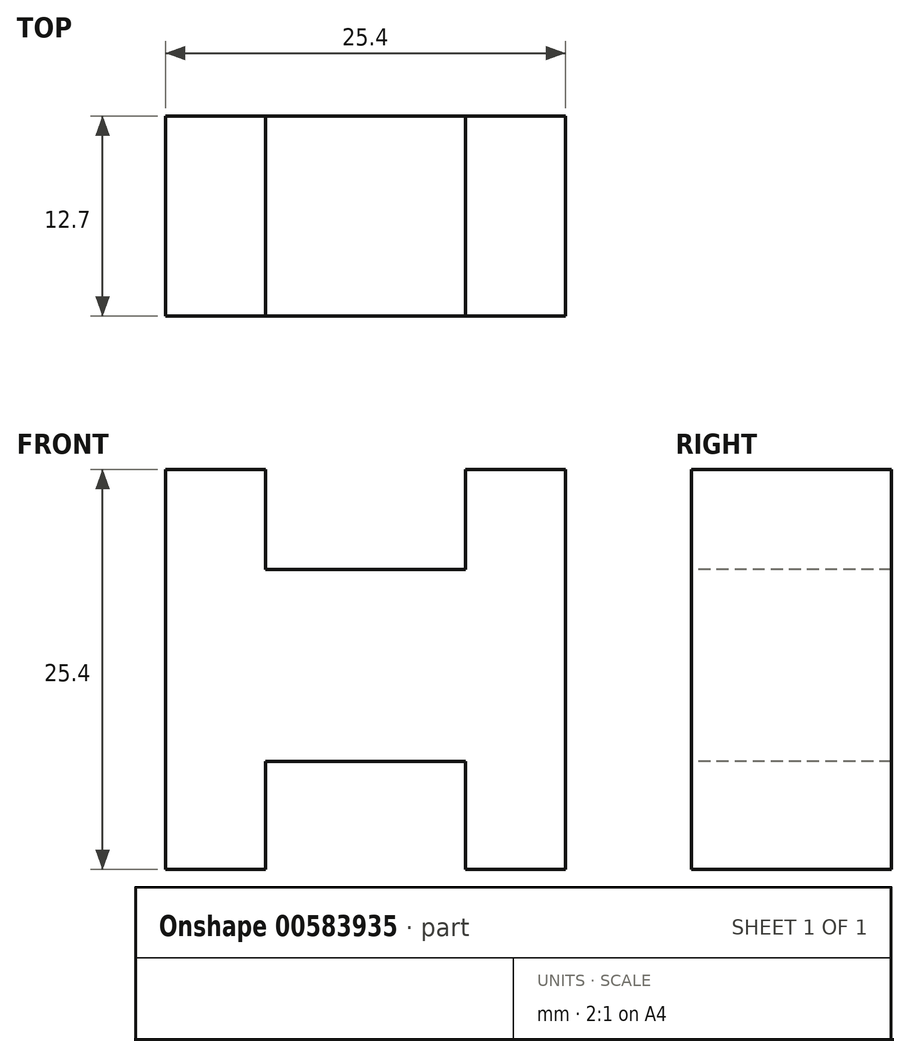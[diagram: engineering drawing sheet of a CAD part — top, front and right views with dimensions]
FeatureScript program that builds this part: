
annotation { "Feature Type Name" : "Feature", "Feature Type Description" : "" }
export const myFeature = defineFeature(function(context is Context, id is Id, definition is map)
    precondition{}
    {
        {
            var Q0;
            Q0=qCreatedBy(makeId("Top.planeOp"),FACE);
            var sketch = newSketch(context, id + "F0", { "sketchPlane" : qUnion([Q0])});
            skLineSegment(sketch, "E0.bottom", {"start": v(-12.7, 12.7) * mm, "end": v(12.7, 12.7) * mm});
            skLineSegment(sketch, "E0.top", {"start": v(-12.7, -12.7) * mm, "end": v(12.7, -12.7) * mm});
            skLineSegment(sketch, "E0.left", {"start": v(-12.7, 12.7) * mm, "end": v(-12.7, -12.7) * mm});
            skLineSegment(sketch, "E0.right", {"start": v(12.7, 12.7) * mm, "end": v(12.7, -12.7) * mm});
            skPoint(sketch, "E0.middle", {"position": v(0, 0) * mm});
            skSolve(sketch);
        }
        {
            var Q0;
            Q0=makeQuery(id+"F0.imprint","IMPRINT",FACE,{"disambiguationData":[TD([[makeQuery(id+"F0.imprint","IMPRINT",EDGE,{"derivedFrom":sQuery(id+"F0.wireOp",EDGE,"E0.bottom")}),-1.0]])]});
            extrude(context, id + "F1", {"entities" : qUnion([Q0]), "depth" : 25.4 * mm, "offsetDistance" : 25.4 * mm});
        }
        {
            var Q0;
            Q0=makeQuery(id+"F1.opExtrude","SWEPT_FACE",FACE,{"disambiguationData":[OSD([sQuery(id+"F0.wireOp",EDGE,"E0.top")])]});
            var sketch = newSketch(context, id + "F2", { "sketchPlane" : qUnion([Q0])});
            skLineSegment(sketch, "E1.bottom", {"start": v(-6.35, 25.4) * mm, "end": v(6.35, 25.4) * mm});
            skLineSegment(sketch, "E1.top", {"start": v(-6.35, 19.05) * mm, "end": v(6.35, 19.05) * mm});
            skLineSegment(sketch, "E1.left", {"start": v(-6.35, 25.4) * mm, "end": v(-6.35, 19.05) * mm});
            skLineSegment(sketch, "E1.right", {"start": v(6.35, 25.4) * mm, "end": v(6.35, 19.05) * mm});
            skSolve(sketch);
        }
        {
            var Q0;
            Q0=makeQuery(id+"F2.imprint","IMPRINT",FACE,{"disambiguationData":[TD([[makeQuery(id+"F2.imprint","IMPRINT",EDGE,{"derivedFrom":sQuery(id+"F2.wireOp",EDGE,"E1.bottom")}),-1.0]])]});
            extrude(context, id + "F3", {"entities" : qUnion([Q0]), "operationType" : NewBodyOperationType.REMOVE, "oppositeDirection" : true, "depth" : 25.4 * mm, "offsetDistance" : 25.4 * mm});
        }
        {
            var Q0;
            Q0=makeQuery(id+"F1.opExtrude","SWEPT_FACE",FACE,{"disambiguationData":[OSD([sQuery(id+"F0.wireOp",EDGE,"E0.top")])]});
            var sketch = newSketch(context, id + "F4", { "sketchPlane" : qUnion([Q0])});
            skLineSegment(sketch, "E2.bottom", {"start": v(-6.35, 0) * mm, "end": v(6.35, 0) * mm});
            skLineSegment(sketch, "E2.top", {"start": v(-6.35, 6.85) * mm, "end": v(6.35, 6.85) * mm});
            skLineSegment(sketch, "E2.left", {"start": v(-6.35, 0) * mm, "end": v(-6.35, 6.85) * mm});
            skLineSegment(sketch, "E2.right", {"start": v(6.35, 0) * mm, "end": v(6.35, 6.85) * mm});
            skSolve(sketch);
        }
        {
            var Q0;
            Q0=makeQuery(id+"F4.imprint","IMPRINT",FACE,{"disambiguationData":[TD([[makeQuery(id+"F4.imprint","IMPRINT",EDGE,{"derivedFrom":sQuery(id+"F4.wireOp",EDGE,"E2.bottom")}),1.0]])]});
            extrude(context, id + "F5", {"entities" : qUnion([Q0]), "operationType" : NewBodyOperationType.REMOVE, "oppositeDirection" : true, "depth" : 25.4 * mm, "offsetDistance" : 25.4 * mm});
        }
        {
            var Q0;
            Q0=makeQuery(id+"F1.opExtrude","SWEPT_FACE",FACE,{"disambiguationData":[OSD([sQuery(id+"F0.wireOp",EDGE,"E0.top")])]});
            extrude(context, id + "F6", {"entities" : qUnion([Q0]), "operationType" : NewBodyOperationType.REMOVE, "oppositeDirection" : true, "depth" : 12.7 * mm, "offsetDistance" : 25.4 * mm});
        }
    });
